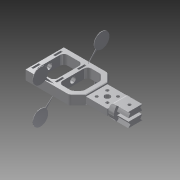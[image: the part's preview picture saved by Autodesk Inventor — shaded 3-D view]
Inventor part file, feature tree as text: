
AUTODESK INVENTOR PART (.ipt)
format: ipt  version: 2014 (Build 180170000, 170)  size: 447,488 bytes
history: native  units: mm
features: extrude x9, sketch x8, fillet x4, plane x2, mirror x2, projected_geometry x2, pattern_linear x1
ambient origin geometry x8: Origin, YZ Plane, XZ Plane, XY Plane, X Axis, Y Axis, Z Axis, Center Point
bodies: Solid1 (feature_tree)
feature tree (28):
  plane  "Work Plane1"
  extrude  "Extrusion7"  Depth=5.0mm
  extrude  "Extrusion8"  Depth=28.0mm
  extrude  "Extrusion9"  Depth=28.0mm
  fillet  "Fillet1"  Radius=22.5mm
  fillet  "Fillet4"  Radius=7.35mm
  sketch  "Sketch11"  dims[d55=14.0mm d56=14.0mm d59=14.0mm d63=4.0mm]
  extrude  "Extrusion10"  Depth=4.0mm
  extrude  "Extrusion13"  Depth=4.0mm
  fillet  "Fillet8"  Radius=4.0mm
  fillet  "Fillet9"  Radius=14.0mm
  extrude  "Extrusion15"  Depth=13.9192mm
  extrude  "Extrusion16"  Depth=6.0mm
  pattern_linear  "Rectangular Pattern1"  Spacing1=6.0mm  [1 undecoded]
  plane  "Work Plane3"
  extrude  "Extrusion17"  TaperAngle=135.0deg  [1 undecoded]
  mirror  "Mirror1"
  mirror  "Mirror2"
  extrude  "Extrusion11"  TaperAngle=135.0deg  [1 undecoded]
  sketch  "Sketch8"  dims[d0=5.0mm d6=4.4mm d12=4.4mm d14=4.4mm]
  sketch  "Sketch9"  dims[d49=7.2mm d50=28.0mm]
  projected_geometry  "Projected Loop1"
  projected_geometry  "Projected Loop2"
  sketch  "Sketch10"  dims[d51=14.0mm d52=28.0mm d53=22.5mm d54=7.35mm]
  sketch  "Sketch12"  dims[d64=4.0mm d65=4.0mm d66=4.0mm d71=14.0mm]
  sketch  "Sketch14"  dims[d72=14.0mm d73=13.9192mm]
  sketch  "Sketch15"  dims[d74=8.0mm d75=0.0mm d76=6.0mm]
  sketch  "Sketch16"  dims[d77=6.0mm d78=6.0mm d79=135.0deg d80=135.0deg d84=38.1mm d85=6.0mm d86=6.0mm d90=127.9977mm d91=25.0mm d92=25.0mm d93=6.0mm d94=6.0mm d95=19.05mm d96=12.35mm d97=0.0mm d98=7.35mm d99=25.05mm d100=25.05mm d101=6.175mm d102=6.175mm d103=5.0mm d105=65.0mm d106=0.0mm d108=1.0mm d109=4.0mm d110=4.0mm d111=26.0mm d112=4.0mm d113=2.0mm d114=2.0mm d115=45.0deg d116=45.0deg d117=22.5mm d118=0.0mm d119=4.0mm d120=2.0mm d121=18.384776mm d122=22.384776mm d123=0.0mm d127=15.0mm d128=0.0mm d139=1.0mm d140=4.0mm d141=1.0mm d149=13.9192mm d150=6.9596mm d151=6.9596mm d152=6.9596mm d153=6.9596mm d154=7.5mm d155=4.0mm d156=20.0mm d157=0.0mm d159=5.6875mm d160=5.6875mm d161=5.6875mm d163=10.0mm d167=2.5mm d168=15.0mm d169=0.0mm d170=20.0mm d172=31.0mm d173=5.6875mm d174=5.6875mm d175=10.0mm d176=1.75mm d177=1.75mm d178=-84.5mm d179=15.0mm d180=15.0mm d181=10.0mm d182=1.570796mm d183=7.068583mm d184=22.5mm d185=0.6mm d186=0.0mm]
note: 3 required parameter values undecoded (feature->parameter linkage not recoverable at this tier; creation-order binding heuristic only, values carry confidence <= 0.55)
